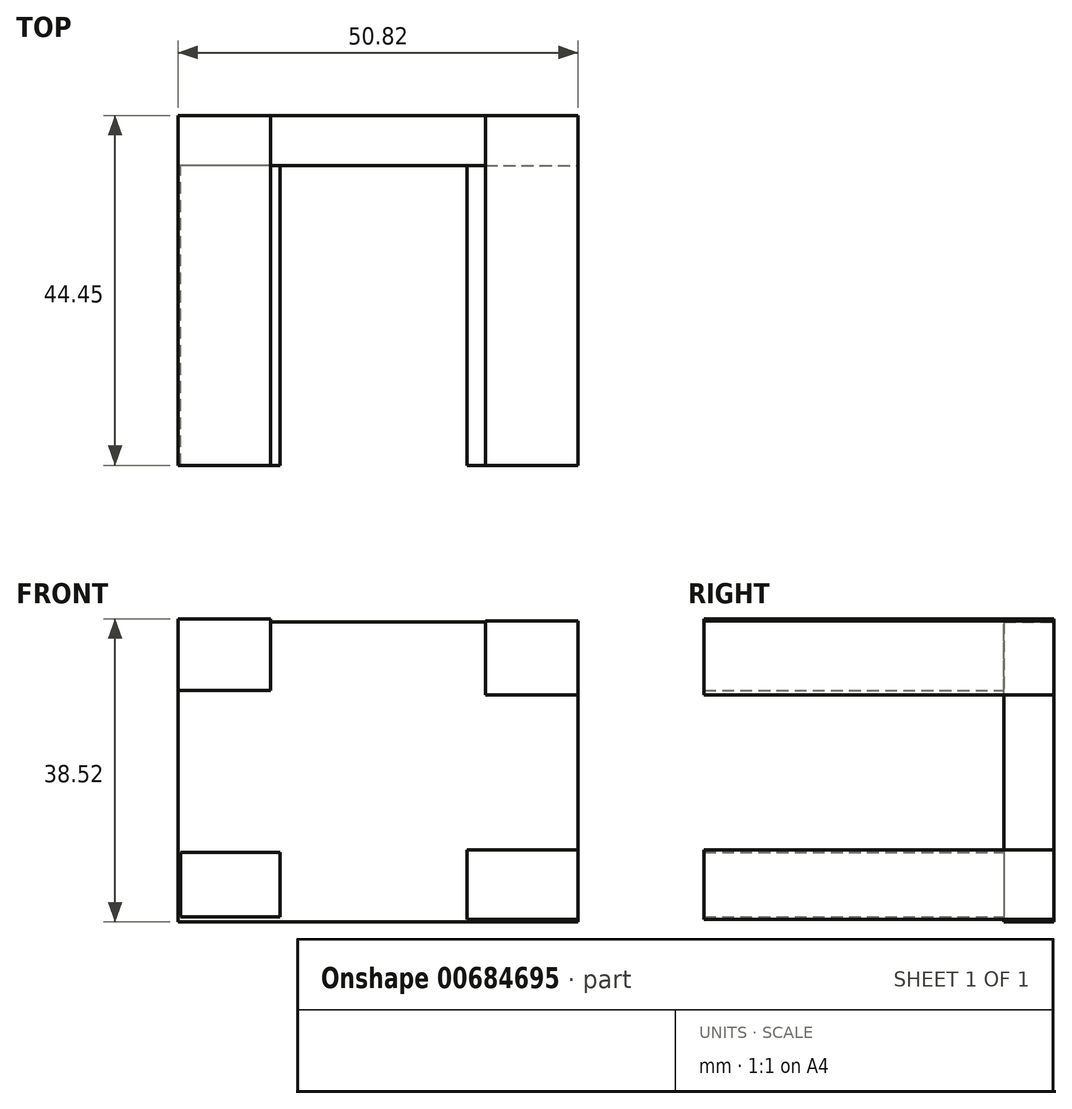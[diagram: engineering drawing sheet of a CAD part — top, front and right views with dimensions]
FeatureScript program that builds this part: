
annotation { "Feature Type Name" : "Feature", "Feature Type Description" : "" }
export const myFeature = defineFeature(function(context is Context, id is Id, definition is map)
    precondition{}
    {
        {
            var Q0;
            Q0=qCreatedBy(makeId("Front.planeOp"),FACE);
            var sketch = newSketch(context, id + "F0", { "sketchPlane" : qUnion([Q0])});
            skLineSegment(sketch, "E0.bottom", {"start": v(-21.3, 22.48) * mm, "end": v(29.5, 22.48) * mm});
            skLineSegment(sketch, "E0.top", {"start": v(-21.3, -15.62) * mm, "end": v(29.5, -15.62) * mm});
            skLineSegment(sketch, "E0.left", {"start": v(-21.3, 22.48) * mm, "end": v(-21.3, -15.62) * mm});
            skLineSegment(sketch, "E0.right", {"start": v(29.5, 22.48) * mm, "end": v(29.5, -15.62) * mm});
            skSolve(sketch);
        }
        {
            var Q0;
            Q0=qSketchRegion(id+"F0",true);
            extrude(context, id + "F1", {"entities" : qUnion([Q0]), "depth" : 6.35 * mm, "offsetDistance" : 25.4 * mm});
        }
        {
            var Q0;
            Q0=qCreatedBy(makeId("Front.planeOp"),FACE);
            var sketch = newSketch(context, id + "F2", { "sketchPlane" : qUnion([Q0])});
            skLineSegment(sketch, "E1.bottom", {"start": v(-21.29, 22.9) * mm, "end": v(-9.54, 22.9) * mm});
            skLineSegment(sketch, "E1.top", {"start": v(-21.29, 13.8) * mm, "end": v(-9.54, 13.8) * mm});
            skLineSegment(sketch, "E1.left", {"start": v(-21.29, 22.9) * mm, "end": v(-21.29, 13.8) * mm});
            skLineSegment(sketch, "E1.right", {"start": v(-9.54, 22.9) * mm, "end": v(-9.54, 13.8) * mm});
            skLineSegment(sketch, "E2.bottom", {"start": v(-21, -14.97) * mm, "end": v(-8.37, -14.97) * mm});
            skLineSegment(sketch, "E2.top", {"start": v(-21, -6.75) * mm, "end": v(-8.37, -6.75) * mm});
            skLineSegment(sketch, "E2.left", {"start": v(-21, -14.97) * mm, "end": v(-21, -6.75) * mm});
            skLineSegment(sketch, "E2.right", {"start": v(-8.37, -14.97) * mm, "end": v(-8.37, -6.75) * mm});
            skLineSegment(sketch, "E3.bottom", {"start": v(29.5, 22.6) * mm, "end": v(17.76, 22.6) * mm});
            skLineSegment(sketch, "E3.top", {"start": v(29.5, 13.21) * mm, "end": v(17.76, 13.21) * mm});
            skLineSegment(sketch, "E3.left", {"start": v(29.5, 22.6) * mm, "end": v(29.5, 13.21) * mm});
            skLineSegment(sketch, "E3.right", {"start": v(17.76, 22.6) * mm, "end": v(17.76, 13.21) * mm});
            skLineSegment(sketch, "E4.bottom", {"start": v(29.5, -15.27) * mm, "end": v(15.41, -15.27) * mm});
            skLineSegment(sketch, "E4.top", {"start": v(29.5, -6.46) * mm, "end": v(15.41, -6.46) * mm});
            skLineSegment(sketch, "E4.left", {"start": v(29.5, -15.27) * mm, "end": v(29.5, -6.46) * mm});
            skLineSegment(sketch, "E4.right", {"start": v(15.41, -15.27) * mm, "end": v(15.41, -6.46) * mm});
            skSolve(sketch);
        }
        {
            var Q0;
            Q0=qSketchRegion(id+"F2",true);
            extrude(context, id + "F3", {"entities" : qUnion([Q0]), "operationType" : NewBodyOperationType.ADD, "depth" : 44.45 * mm, "offsetDistance" : 25.4 * mm});
        }
    });
